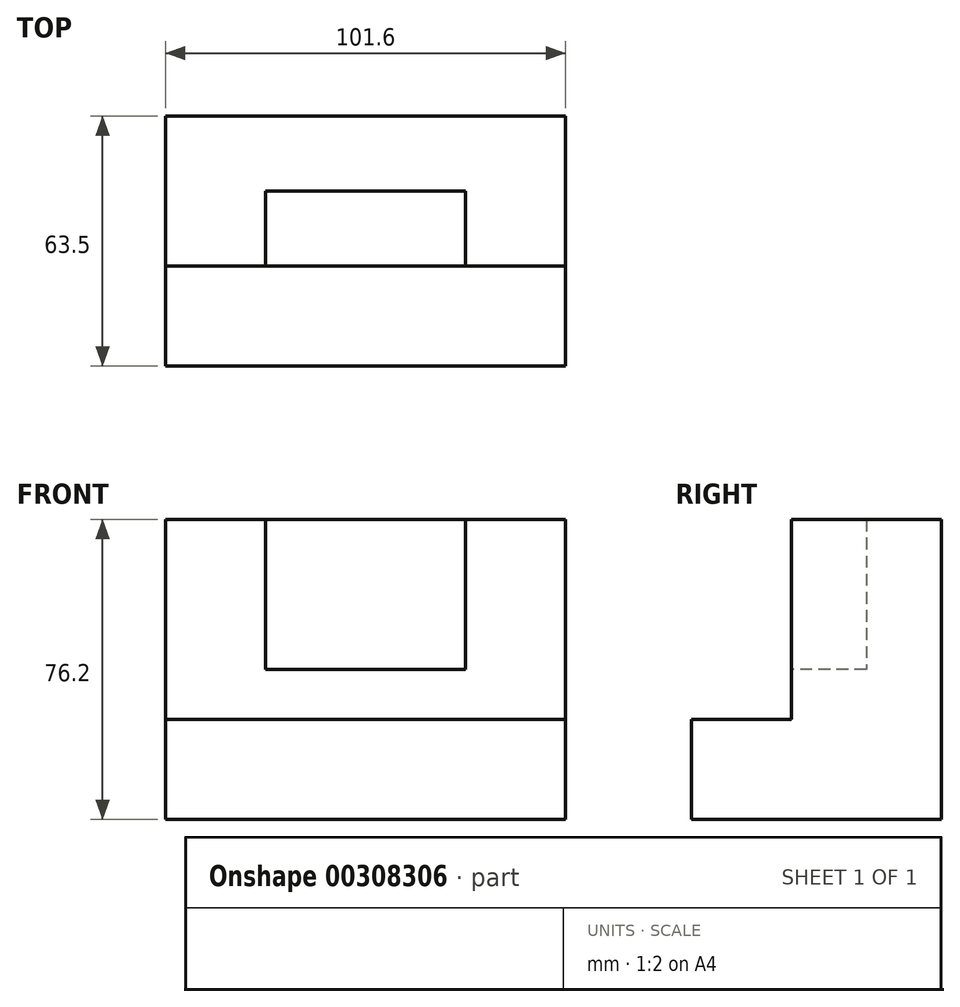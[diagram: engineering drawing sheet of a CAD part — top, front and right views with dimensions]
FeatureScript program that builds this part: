
annotation { "Feature Type Name" : "Feature", "Feature Type Description" : "" }
export const myFeature = defineFeature(function(context is Context, id is Id, definition is map)
    precondition{}
    {
        {
            var Q0;
            Q0=qCreatedBy(makeId("Right.planeOp"),FACE);
            var sketch = newSketch(context, id + "F0", { "sketchPlane" : qUnion([Q0])});
            skLineSegment(sketch, "E0", {"start": v(-35.01, -27.52) * mm, "end": v(28.49, -27.52) * mm});
            skLineSegment(sketch, "E1", {"start": v(-35.01, -27.52) * mm, "end": v(-35.01, -2.12) * mm});
            skLineSegment(sketch, "E2", {"start": v(-35.01, -2.12) * mm, "end": v(-9.61, -2.12) * mm});
            skLineSegment(sketch, "E3", {"start": v(-9.61, -2.12) * mm, "end": v(-9.61, 48.68) * mm});
            skLineSegment(sketch, "E4", {"start": v(-9.61, 48.68) * mm, "end": v(28.49, 48.68) * mm});
            skLineSegment(sketch, "E5", {"start": v(28.49, 48.68) * mm, "end": v(28.49, -27.52) * mm});
            skSolve(sketch);
        }
        {
            var Q0;
            Q0=makeQuery(id+"F0.imprint","IMPRINT",FACE,{"disambiguationData":[TD([[makeQuery(id+"F0.imprint","IMPRINT",EDGE,{"derivedFrom":sQuery(id+"F0.wireOp",EDGE,"E0")}),1.0]])]});
            extrude(context, id + "F1", {"entities" : qUnion([Q0]), "oppositeDirection" : true, "depth" : 101.6 * mm});
        }
        {
            var Q0;
            Q0=makeQuery(id+"F1.opExtrude","SWEPT_FACE",FACE,{"disambiguationData":[OSD([sQuery(id+"F0.wireOp",EDGE,"E3")])]});
            var sketch = newSketch(context, id + "F2", { "sketchPlane" : qUnion([Q0])});
            skLineSegment(sketch, "E6.bottom", {"start": v(-76.2, 48.68) * mm, "end": v(-25.4, 48.68) * mm});
            skLineSegment(sketch, "E6.top", {"start": v(-76.2, 10.58) * mm, "end": v(-25.4, 10.58) * mm});
            skLineSegment(sketch, "E6.left", {"start": v(-76.2, 48.68) * mm, "end": v(-76.2, 10.58) * mm});
            skLineSegment(sketch, "E6.right", {"start": v(-25.4, 48.68) * mm, "end": v(-25.4, 10.58) * mm});
            skSolve(sketch);
        }
        {
            var Q0;
            Q0=makeQuery(id+"F2.imprint","IMPRINT",FACE,{"disambiguationData":[TD([[makeQuery(id+"F2.imprint","IMPRINT",EDGE,{"derivedFrom":sQuery(id+"F2.wireOp",EDGE,"E6.bottom")}),-1.0]])]});
            extrude(context, id + "F3", {"entities" : qUnion([Q0]), "operationType" : NewBodyOperationType.REMOVE, "oppositeDirection" : true, "depth" : 19.05 * mm});
        }
    });
